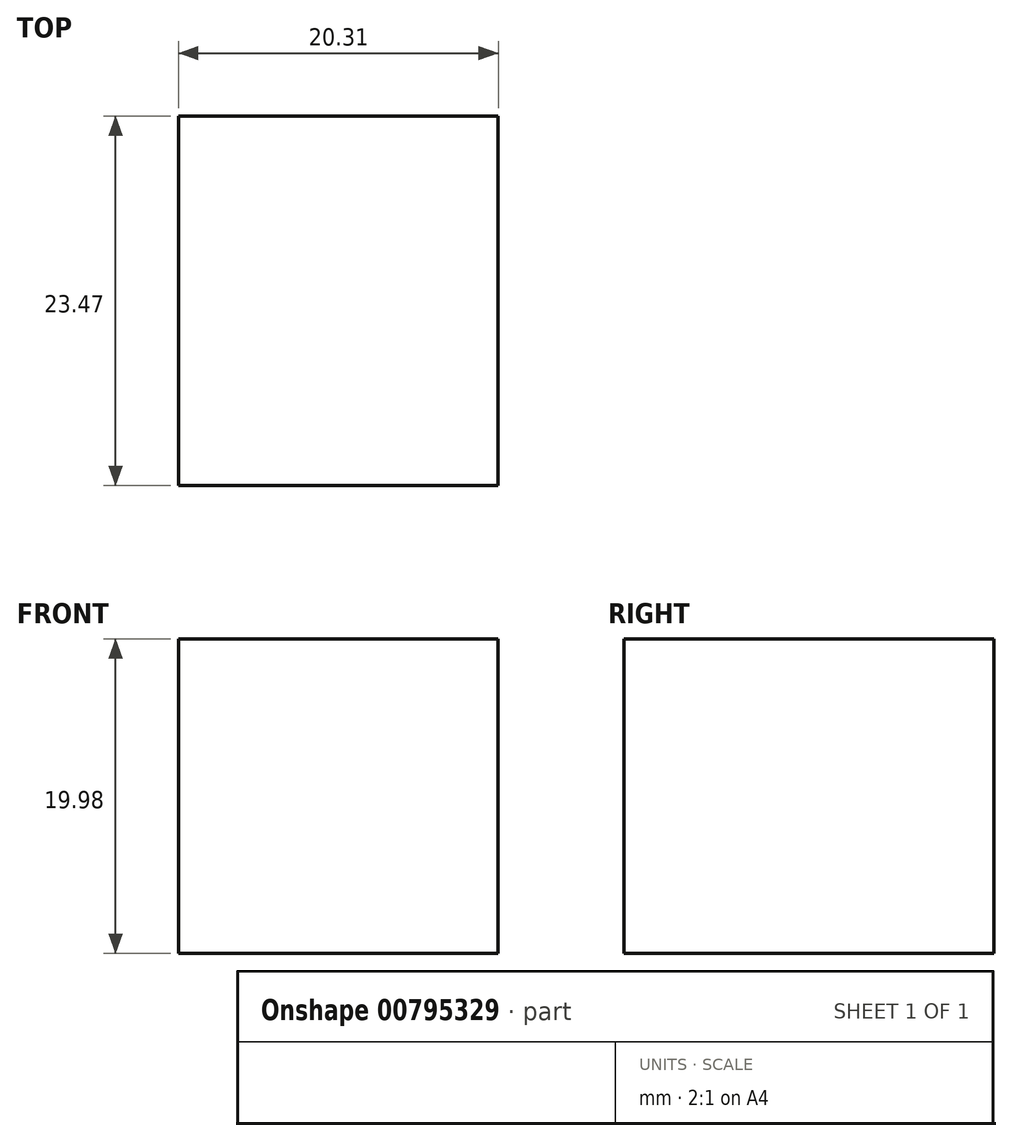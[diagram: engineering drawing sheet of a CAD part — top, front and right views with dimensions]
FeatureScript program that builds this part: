
annotation { "Feature Type Name" : "Feature", "Feature Type Description" : "" }
export const myFeature = defineFeature(function(context is Context, id is Id, definition is map)
    precondition{}
    {
        {
            var Q0;
            Q0=qCreatedBy(makeId("Front.planeOp"),FACE);
            var sketch = newSketch(context, id + "F0", { "sketchPlane" : qUnion([Q0])});
            skLineSegment(sketch, "E0.bottom", {"start": v(-47.31, 10.4) * mm, "end": v(-27, 10.4) * mm});
            skLineSegment(sketch, "E0.top", {"start": v(-47.31, -9.58) * mm, "end": v(-27, -9.58) * mm});
            skLineSegment(sketch, "E0.left", {"start": v(-47.31, 10.4) * mm, "end": v(-47.31, -9.58) * mm});
            skLineSegment(sketch, "E0.right", {"start": v(-27, 10.4) * mm, "end": v(-27, -9.58) * mm});
            skSolve(sketch);
        }
        {
            var Q0;
            Q0 = qSketchRegion(id + "F0", true);
            extrude(context, id + "F1", {"entities" : qUnion([Q0]), "depth" : 23.47 * mm, "offsetDistance" : 30.48 * mm});
        }
    });
